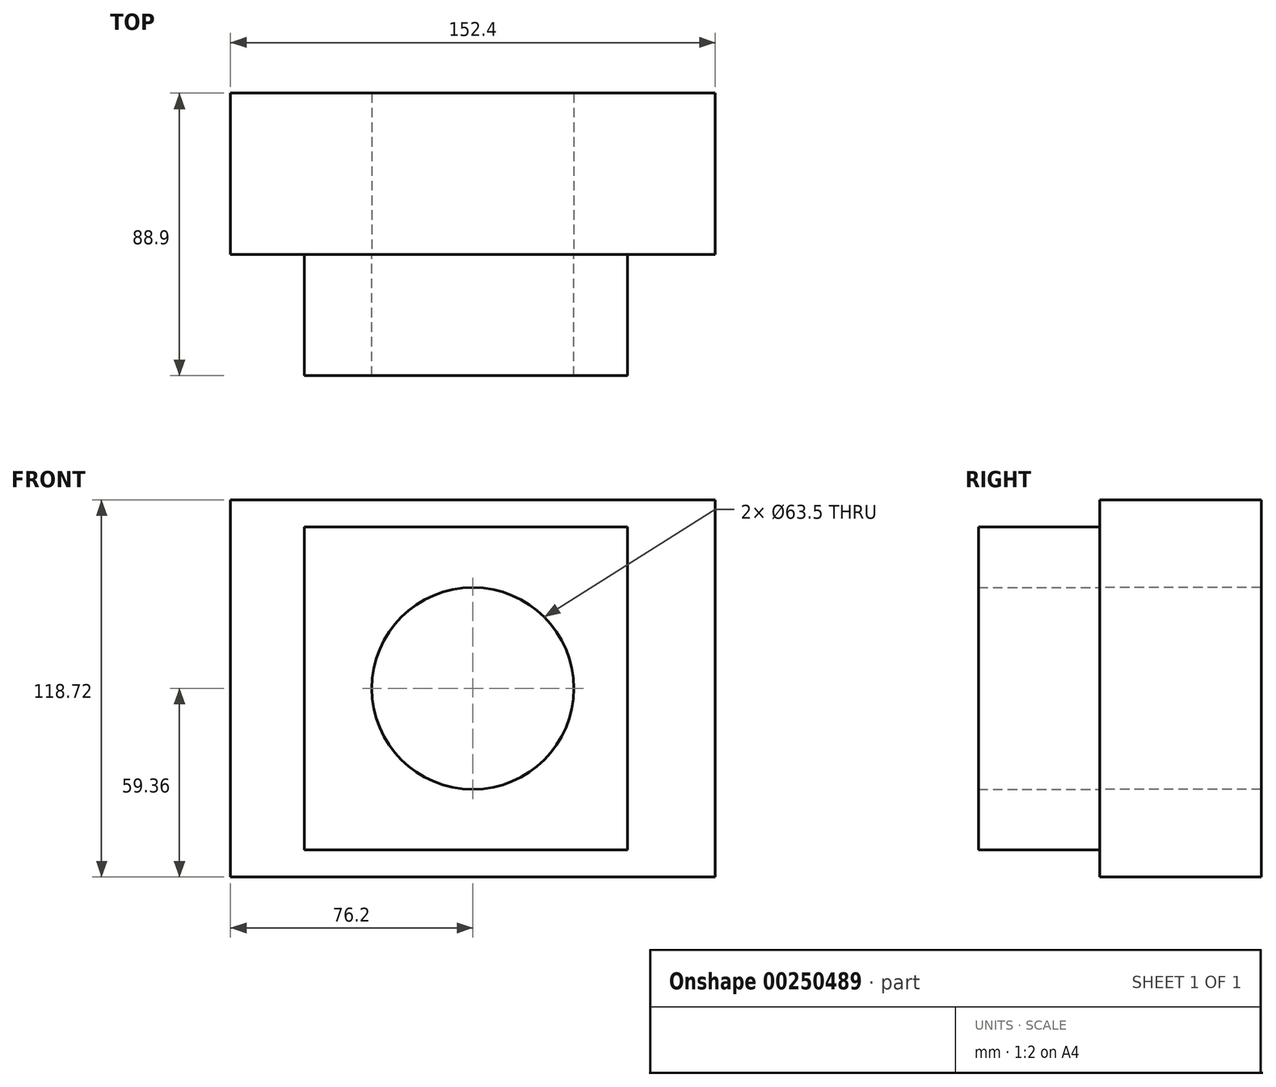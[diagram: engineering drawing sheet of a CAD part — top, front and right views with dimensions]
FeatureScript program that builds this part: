
annotation { "Feature Type Name" : "Feature", "Feature Type Description" : "" }
export const myFeature = defineFeature(function(context is Context, id is Id, definition is map)
    precondition{}
    {
        {
            var Q0;
            Q0=qCreatedBy(makeId("Front.planeOp"),FACE);
            var sketch = newSketch(context, id + "F0", { "sketchPlane" : qUnion([Q0])});
            skCircle(sketch, "E0", {"center": v(0, 0) * mm, "radius": 31.75 * mm});
            skLineSegment(sketch, "E1.bottom", {"start": v(48.59, 50.8) * mm, "end": v(-53.01, 50.8) * mm});
            skLineSegment(sketch, "E1.top", {"start": v(48.59, -50.8) * mm, "end": v(-53.01, -50.8) * mm});
            skLineSegment(sketch, "E1.left", {"start": v(48.59, 50.8) * mm, "end": v(48.59, -50.8) * mm});
            skLineSegment(sketch, "E1.right", {"start": v(-53.01, 50.8) * mm, "end": v(-53.01, -50.8) * mm});
            skPoint(sketch, "E1.middle", {"position": v(-2.21, 0) * mm});
            skLineSegment(sketch, "E2.bottom", {"start": v(76.2, 59.36) * mm, "end": v(-76.2, 59.36) * mm});
            skLineSegment(sketch, "E2.top", {"start": v(76.2, -59.36) * mm, "end": v(-76.2, -59.36) * mm});
            skLineSegment(sketch, "E2.left", {"start": v(76.2, 59.36) * mm, "end": v(76.2, -59.36) * mm});
            skLineSegment(sketch, "E2.right", {"start": v(-76.2, 59.36) * mm, "end": v(-76.2, -59.36) * mm});
            skSolve(sketch);
        }
        {
            var Q0;
            Q0=makeQuery(id+"F0.imprint","IMPRINT",FACE,{"disambiguationData":[TD([[makeQuery(id+"F0.imprint","IMPRINT",EDGE,{"derivedFrom":sQuery(id+"F0.wireOp",EDGE,"E0")}),-1.0]])]});
            extrude(context, id + "F1", {"entities" : qUnion([Q0]), "depth" : 38.1 * mm});
        }
        {
            var Q0;
            Q0=makeQuery(id+"F0.imprint","IMPRINT",FACE,{"disambiguationData":[TD([[makeQuery(id+"F0.imprint","IMPRINT",EDGE,{"derivedFrom":sQuery(id+"F0.wireOp",EDGE,"E1.bottom")}),-1.0]])]});
            var Q1;
            Q1=makeQuery(id+"F0.imprint","IMPRINT",FACE,{"disambiguationData":[TD([[makeQuery(id+"F0.imprint","IMPRINT",EDGE,{"derivedFrom":sQuery(id+"F0.wireOp",EDGE,"E0")}),-1.0]])]});
            extrude(context, id + "F2", {"entities" : qUnion([Q0, Q1]), "oppositeDirection" : true, "depth" : 50.8 * mm});
        }
    });
